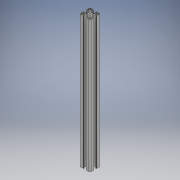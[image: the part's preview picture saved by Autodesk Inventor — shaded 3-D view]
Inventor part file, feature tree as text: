
AUTODESK INVENTOR PART (.ipt)
format: ipt  version: 2019 (Build 230136000, 136)  size: 297,472 bytes
history: native  units: mm
features: extrude x1, sketch x1
ambient origin geometry x8: Origin, YZ Plane, XZ Plane, XY Plane, X Axis, Y Axis, Z Axis, Center Point
bodies: Solid1 (feature_tree)
feature tree (2):
  extrude  "Extrusion1"  Depth=500.0mm
  sketch  "Sketch1"  dims[d0=4.1mm d1=5.1mm d2=6.4mm d3=7.4mm d4=9.25mm d5=10.25mm d6=11.55mm d7=12.55mm d8=15.5mm d9=18.5mm d10=20.0mm d11=17.5mm d12=500.0mm d13=0.0mm d15=6.8mm]
